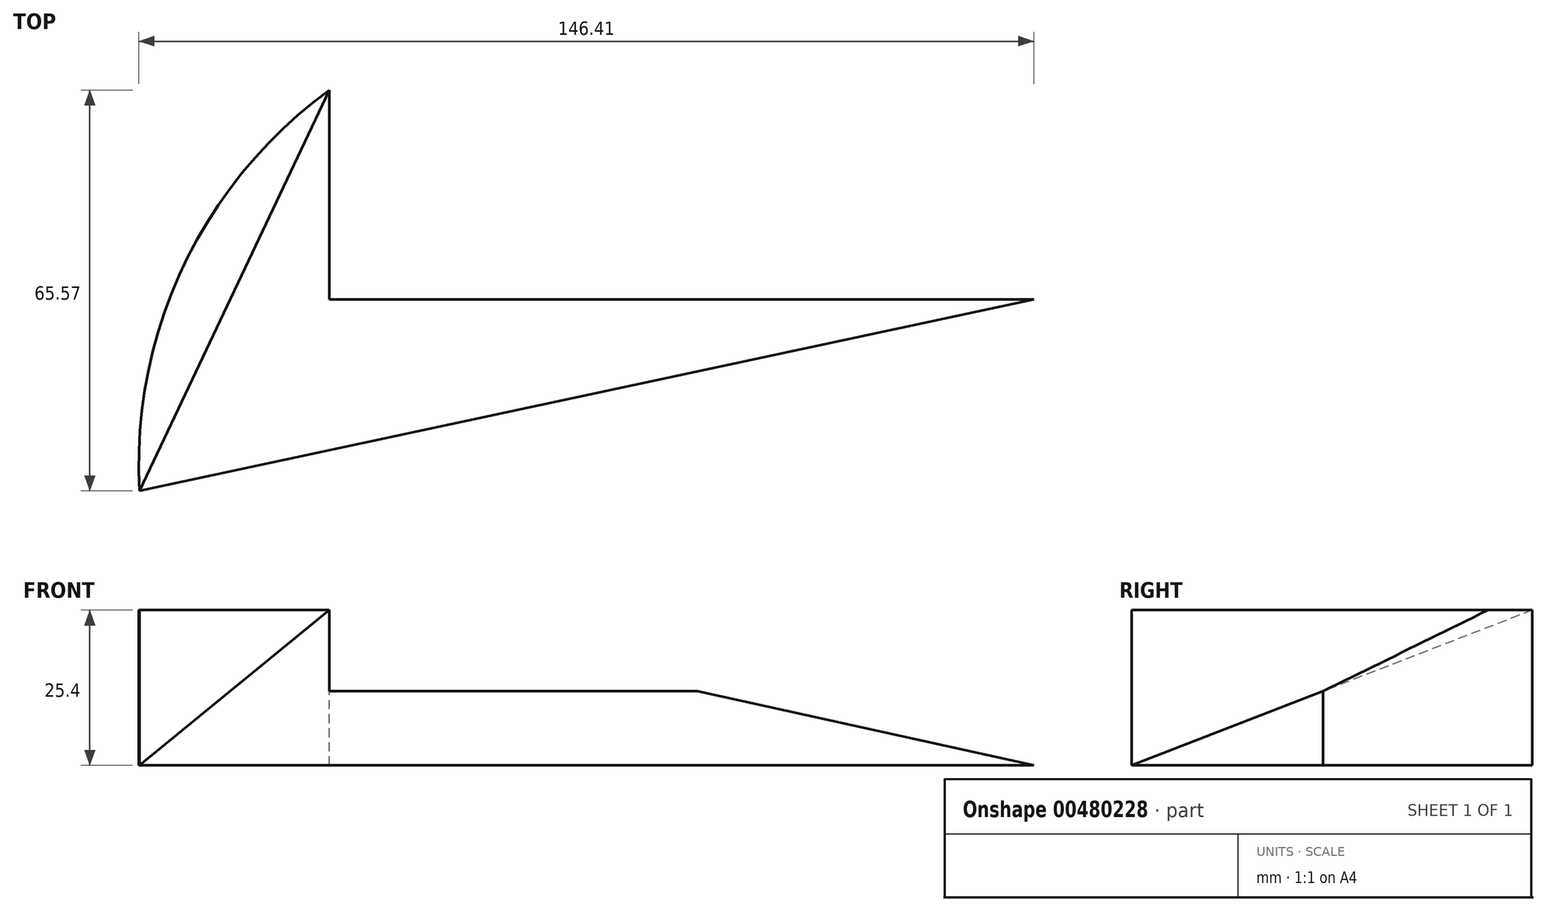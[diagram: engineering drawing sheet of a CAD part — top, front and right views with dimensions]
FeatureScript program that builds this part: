
annotation { "Feature Type Name" : "Feature", "Feature Type Description" : "" }
export const myFeature = defineFeature(function(context is Context, id is Id, definition is map)
    precondition{}
    {
        {
            var Q0;
            Q0=qCreatedBy(makeId("Top.planeOp"),FACE);
            var sketch = newSketch(context, id + "F0", { "sketchPlane" : qUnion([Q0])});
            skLineSegment(sketch, "E0", {"start": v(-146.28, -31.13) * mm, "end": v(0, 0.18) * mm});
            skLineSegment(sketch, "E1", {"start": v(0, 0.18) * mm, "end": v(-115.22, 34.44) * mm});
            skLineSegment(sketch, "E2", {"start": v(-115.22, 34.44) * mm, "end": v(-146.28, -31.13) * mm});
            skArc(sketch, "E3", {"start": v(0, 0.18) * mm, "mid": v(-86.56, 47.23) * mm, "end": v(-146.28, -31.13) * mm});
            skSolve(sketch);
        }
        {
            var Q0;
            {var subQ0=sQuery(id+"F0.wireOp",EDGE,"E2");Q0=makeQuery(id+"F0.imprint","IMPRINT",FACE,{"disambiguationData":[TD([[makeQuery(id+"F0.imprint","IMPRINT",EDGE,{"derivedFrom":subQ0}),-1.0]])]});}
            var Q1;
            Q1=makeQuery(id+"F0.imprint","IMPRINT",FACE,{"disambiguationData":[TD([[makeQuery(id+"F0.imprint","IMPRINT",EDGE,{"derivedFrom":sQuery(id+"F0.wireOp",EDGE,"E0")}),1.0]])]});
            extrude(context, id + "F1", {"entities" : qUnion([Q0, Q1]), "depth" : 25.4 * mm});
        }
        {
            var Q0;
            Q0=makeQuery(id+"F1.opExtrude","CAP_FACE",FACE,{"disambiguationData":[OSD([sQuery(id+"F0.wireOp",EDGE,"E0"),sQuery(id+"F0.wireOp",EDGE,"E1"),sQuery(id+"F0.wireOp",EDGE,"E3")])],"isStart":false});
            var sketch = newSketch(context, id + "F2", { "sketchPlane" : qUnion([Q0])});
            skLineSegment(sketch, "E4.bottom", {"start": v(-115.22, 34.44) * mm, "end": v(0, 34.44) * mm});
            skLineSegment(sketch, "E4.top", {"start": v(-115.22, 0.18) * mm, "end": v(0, 0.18) * mm});
            skLineSegment(sketch, "E4.left", {"start": v(-115.22, 34.44) * mm, "end": v(-115.22, 0.18) * mm});
            skLineSegment(sketch, "E4.right", {"start": v(0, 34.44) * mm, "end": v(0, 0.18) * mm});
            skSolve(sketch);
        }
        {
            var Q0;
            Q0 = qSketchRegion(id + "F2", true);
            extrude(context, id + "F3", {"entities" : qUnion([Q0]), "operationType" : NewBodyOperationType.REMOVE, "oppositeDirection" : true, "depth" : 25.4 * mm});
        }
        {
            var Q0;
            Q0=makeQuery(id+"F1.opExtrude","CAP_FACE",FACE,{"disambiguationData":[OSD([sQuery(id+"F0.wireOp",EDGE,"E0"),sQuery(id+"F0.wireOp",EDGE,"E1"),sQuery(id+"F0.wireOp",EDGE,"E3")])],"isStart":false});
            var Q1;
            Q1=makeQuery(id+"F1.opExtrude","SWEPT_FACE",FACE,{"disambiguationData":[OSD([sQuery(id+"F0.wireOp",EDGE,"E0")])]});
            loft(context, id + "F4", {"operationType" : NewBodyOperationType.REMOVE, "sheetProfilesArray" : [{ "sheetProfileEntities" : qUnion([Q0]) }, { "sheetProfileEntities" : qUnion([Q1]) }]});
        }
    });
